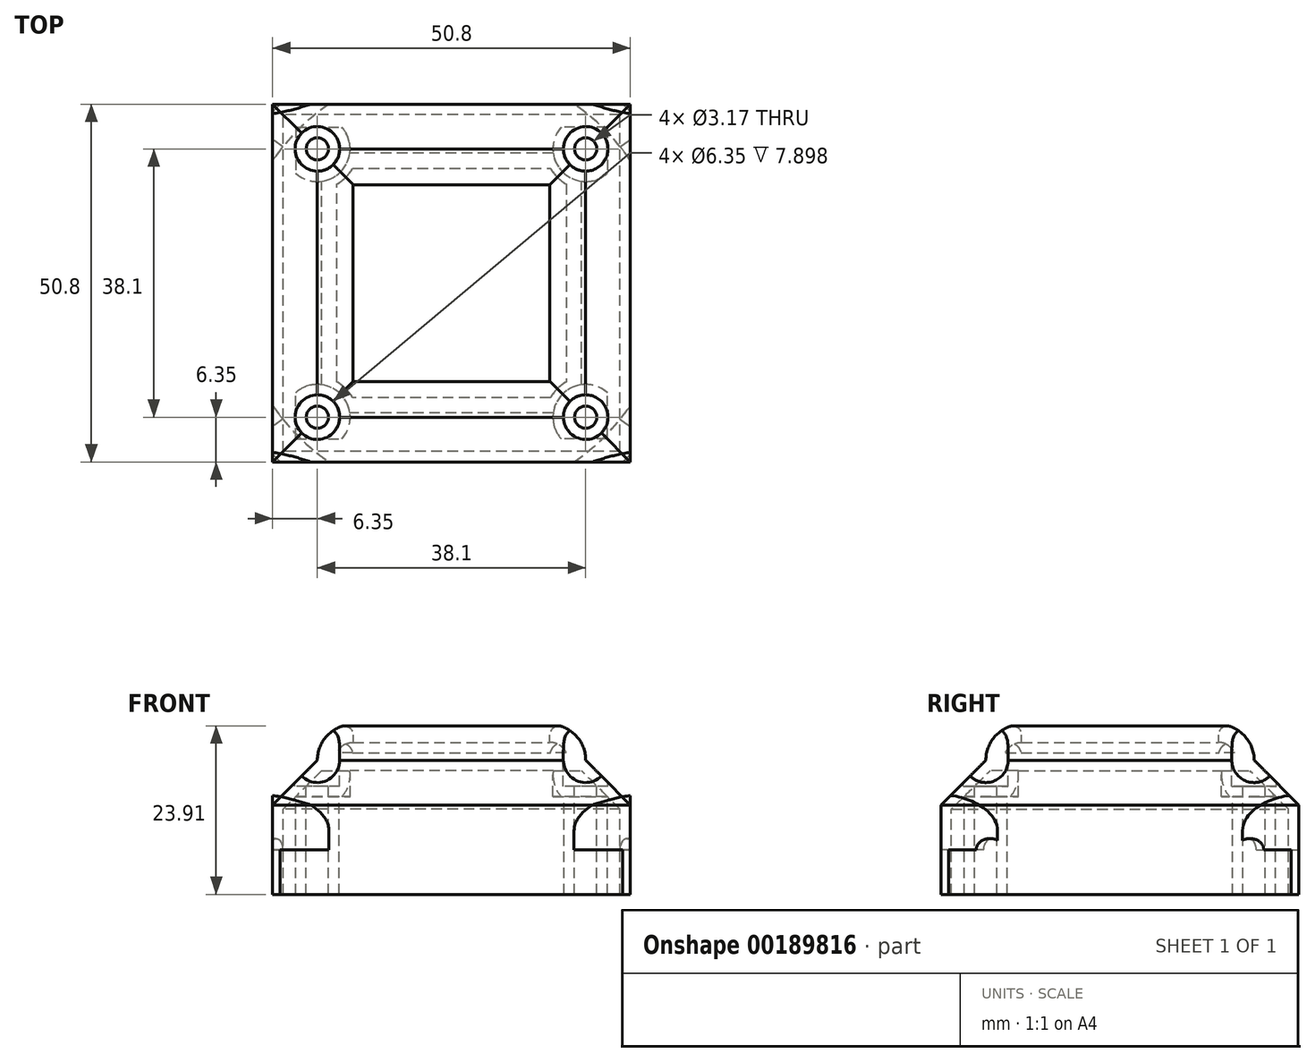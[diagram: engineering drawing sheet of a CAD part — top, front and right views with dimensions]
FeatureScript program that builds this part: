
annotation { "Feature Type Name" : "Feature", "Feature Type Description" : "" }
export const myFeature = defineFeature(function(context is Context, id is Id, definition is map)
    precondition{}
    {
        {
            var Q0;
            Q0=qCreatedBy(makeId("Front.planeOp"),FACE);
            var sketch = newSketch(context, id + "F0", { "sketchPlane" : qUnion([Q0])});
            skLineSegment(sketch, "E0.bottom", {"start": v(30.79, -7.77) * mm, "end": v(-30.79, -7.77) * mm});
            skLineSegment(sketch, "E0.top", {"start": v(30.79, 7.77) * mm, "end": v(-30.79, 7.77) * mm});
            skLineSegment(sketch, "E0.left", {"start": v(30.79, -7.77) * mm, "end": v(30.79, 7.77) * mm});
            skLineSegment(sketch, "E0.right", {"start": v(-30.79, -7.77) * mm, "end": v(-30.79, 7.77) * mm});
            skPoint(sketch, "E0.middle", {"position": v(0, 0) * mm});
            skLineSegment(sketch, "E1.bottom", {"start": v(30.79, 7.77) * mm, "end": v(39.54, 7.77) * mm});
            skLineSegment(sketch, "E1.top", {"start": v(30.79, -14.83) * mm, "end": v(39.54, -14.83) * mm});
            skLineSegment(sketch, "E1.left", {"start": v(30.79, 7.77) * mm, "end": v(30.79, -14.83) * mm});
            skLineSegment(sketch, "E1.right", {"start": v(39.54, 7.77) * mm, "end": v(39.54, -14.83) * mm});
            skLineSegment(sketch, "E2", {"start": v(30.79, -7.77) * mm, "end": v(39.54, -7.77) * mm});
            skLineSegment(sketch, "E3", {"start": v(0, 7.77) * mm, "end": v(0, -7.77) * mm});
            skLineSegment(sketch, "E4", {"start": v(-30.79, 0) * mm, "end": v(0, 0) * mm});
            skLineSegment(sketch, "E5", {"start": v(30.79, 0) * mm, "end": v(39.54, 0) * mm});
            skCircle(sketch, "E6", {"center": v(0, 0) * mm, "radius": 3.17 * mm});
            skLineSegment(sketch, "E7", {"start": v(35.16, 0) * mm, "end": v(35.16, -7.77) * mm});
            skLineSegment(sketch, "E8", {"start": v(39.54, -3.53) * mm, "end": v(35.16, -3.53) * mm});
            skSolve(sketch);
        }
        {
            var Q0;
            {var subQ1=sQuery(id+"F0.wireOp",EDGE,"E1.bottom");Q0=makeQuery(id+"F0.imprint","IMPRINT",FACE,{"disambiguationData":[TD([[makeQuery(id+"F0.imprint","IMPRINT",EDGE,{"derivedFrom":subQ1}),-1.0]])]});}
            var Q1;
            {var subQ5=sQuery(id+"F0.wireOp",EDGE,"E7");Q1=makeQuery(id+"F0.imprint","IMPRINT",FACE,{"disambiguationData":[TD([[makeQuery(id+"F0.imprint","IMPRINT",EDGE,{"derivedFrom":subQ5}),1.0]])]});}
            var Q2;
            {var subQ4=sQuery(id+"F0.wireOp",EDGE,"E1.top");Q2=makeQuery(id+"F0.imprint","IMPRINT",FACE,{"disambiguationData":[TD([[makeQuery(id+"F0.imprint","IMPRINT",EDGE,{"derivedFrom":subQ4}),1.0]])]});}
            var Q3;
            Q3=sQuery(id+"F0.wireOp",EDGE,"E3");
            revolve(context, id + "F1", {"entities" : qUnion([Q0, Q1, Q2]), "axis" : qUnion([Q3]), "revolveType" : RevolveType.SYMMETRIC, "angle" : 36 * degree});
        }
        {
            var Q0;
            {var subQ5=sQuery(id+"F0.wireOp",EDGE,"E1.bottom");Q0=makeQuery(id+"F0.imprint","IMPRINT",FACE,{"disambiguationData":[TD([[makeQuery(id+"F0.imprint","IMPRINT",EDGE,{"derivedFrom":subQ5}),-1.0]])]});}
            var Q1;
            {var subQ3=sQuery(id+"F0.wireOp",EDGE,"E8");Q1=makeQuery(id+"F0.imprint","IMPRINT",FACE,{"disambiguationData":[TD([[makeQuery(id+"F0.imprint","IMPRINT",EDGE,{"derivedFrom":subQ3}),-1.0]])]});}
            var Q2;
            {var subQ3=sQuery(id+"F0.wireOp",EDGE,"E8");Q2=makeQuery(id+"F0.imprint","IMPRINT",FACE,{"disambiguationData":[TD([[makeQuery(id+"F0.imprint","IMPRINT",EDGE,{"derivedFrom":subQ3}),1.0]])]});}
            var Q3;
            {var subQ5=sQuery(id+"F0.wireOp",EDGE,"E1.top");Q3=makeQuery(id+"F0.imprint","IMPRINT",FACE,{"disambiguationData":[TD([[makeQuery(id+"F0.imprint","IMPRINT",EDGE,{"derivedFrom":subQ5}),1.0]])]});}
            extrude(context, id + "F2", {"entities" : qUnion([Q0, Q1, Q2, Q3]), "endBound" : BoundingType.SYMMETRIC, "depth" : 25.4 * mm});
        }
        {
            var Q0;
            Q0=makeQuery(id+"F2.opExtrude","SWEPT_FACE",FACE,{"disambiguationData":[OSD([sQuery(id+"F0.wireOp",EDGE,"E1.right")])]});
            var sketch = newSketch(context, id + "F3", { "sketchPlane" : qUnion([Q0])});
            skCircle(sketch, "E9", {"center": v(0, 0) * mm, "radius": 2.98 * mm});
            skSolve(sketch);
        }
        {
            var Q0;
            Q0=sQuery(id+"F3.wireOp",VERTEX,"E9.center");
            var Q1;
            Q1=makeQuery(id+"F1.opRevolve","SWEPT_BODY",BODY,{"disambiguationData":[OSD([sQuery(id+"F0.wireOp",EDGE,"E1.bottom"),sQuery(id+"F0.wireOp",EDGE,"E1.top"),sQuery(id+"F0.wireOp",EDGE,"E1.left"),sQuery(id+"F0.wireOp",EDGE,"E1.right"),sQuery(id+"F0.wireOp",EDGE,"E2"),sQuery(id+"F0.wireOp",EDGE,"E5"),sQuery(id+"F0.wireOp",EDGE,"E7")])]});
            hole(context, id + "F4", {"style" : HoleStyle.C_BORE, "endStyle" : HoleEndStyle.BLIND, "holeDiameter" : 3.17 * mm, "cBoreDiameter" : 6.35 * mm, "cBoreDepth" : 0.5 * mm, "holeDepth" : 12.7 * mm, "locations" : qUnion([Q0]), "scope" : qUnion([Q1])});
        }
        {
            var Q0;
            Q0=makeQuery(id+"F1.opRevolve","SWEPT_BODY",BODY,{"disambiguationData":[OSD([sQuery(id+"F0.wireOp",EDGE,"E1.bottom"),sQuery(id+"F0.wireOp",EDGE,"E1.top"),sQuery(id+"F0.wireOp",EDGE,"E1.left"),sQuery(id+"F0.wireOp",EDGE,"E1.right"),sQuery(id+"F0.wireOp",EDGE,"E2"),sQuery(id+"F0.wireOp",EDGE,"E5"),sQuery(id+"F0.wireOp",EDGE,"E7")])]});
            var Q1;
            Q1=sQuery(id+"F0.wireOp",EDGE,"E3");
            circularPattern(context, id + "F5", {"operationType" : NewBodyOperationType.ADD, "entities" : qUnion([Q0]), "axis" : qUnion([Q1]), "angle" : 36 * degree, "instanceCount" : 10});
        }
        {
            var Q0;
            {var subQ0=makeQuery(id+"F1.opRevolve","SWEPT_EDGE",EDGE,{"disambiguationData":[OSD([sQuery(id+"F0.wireOp",EDGE,"E1.bottom"),sQuery(id+"F0.wireOp",EDGE,"E1.right")])]});Q0=makeQuery(id+"F5.boolean.opBoolean","MERGE",EDGE,{"derivedFrom":[subQ0,makeQuery(id+"F5.opPattern","COPY",EDGE,{"derivedFrom":subQ0,"instanceName":"1"}),makeQuery(id+"F5.opPattern","COPY",EDGE,{"derivedFrom":subQ0,"instanceName":"2"}),makeQuery(id+"F5.opPattern","COPY",EDGE,{"derivedFrom":subQ0,"instanceName":"3"}),makeQuery(id+"F5.opPattern","COPY",EDGE,{"derivedFrom":subQ0,"instanceName":"4"}),makeQuery(id+"F5.opPattern","COPY",EDGE,{"derivedFrom":subQ0,"instanceName":"5"}),makeQuery(id+"F5.opPattern","COPY",EDGE,{"derivedFrom":subQ0,"instanceName":"6"}),makeQuery(id+"F5.opPattern","COPY",EDGE,{"derivedFrom":subQ0,"instanceName":"7"}),makeQuery(id+"F5.opPattern","COPY",EDGE,{"derivedFrom":subQ0,"instanceName":"8"}),makeQuery(id+"F5.opPattern","COPY",EDGE,{"derivedFrom":subQ0,"instanceName":"9"})]});}
            chamfer(context, id + "F6", {"entities" : qUnion([Q0]), "width" : 1.27 * mm, "tangentPropagation" : true});
        }
        {
            var Q0;
            {var subQ0=makeQuery(id+"F1.opRevolve","SWEPT_EDGE",EDGE,{"disambiguationData":[OSD([sQuery(id+"F0.wireOp",EDGE,"E1.top"),sQuery(id+"F0.wireOp",EDGE,"E1.right")])]});Q0=makeQuery(id+"F5.boolean.opBoolean","MERGE",EDGE,{"derivedFrom":[subQ0,makeQuery(id+"F5.opPattern","COPY",EDGE,{"derivedFrom":subQ0,"instanceName":"1"}),makeQuery(id+"F5.opPattern","COPY",EDGE,{"derivedFrom":subQ0,"instanceName":"2"}),makeQuery(id+"F5.opPattern","COPY",EDGE,{"derivedFrom":subQ0,"instanceName":"3"}),makeQuery(id+"F5.opPattern","COPY",EDGE,{"derivedFrom":subQ0,"instanceName":"4"}),makeQuery(id+"F5.opPattern","COPY",EDGE,{"derivedFrom":subQ0,"instanceName":"5"}),makeQuery(id+"F5.opPattern","COPY",EDGE,{"derivedFrom":subQ0,"instanceName":"6"}),makeQuery(id+"F5.opPattern","COPY",EDGE,{"derivedFrom":subQ0,"instanceName":"7"}),makeQuery(id+"F5.opPattern","COPY",EDGE,{"derivedFrom":subQ0,"instanceName":"8"}),makeQuery(id+"F5.opPattern","COPY",EDGE,{"derivedFrom":subQ0,"instanceName":"9"})]});}
            chamfer(context, id + "F7", {"entities" : qUnion([Q0]), "width" : 8.13 * mm, "tangentPropagation" : true});
        }
        {
            var Q0;
            {var subQ0=makeQuery(id+"F1.opRevolve","SWEPT_EDGE",EDGE,{"disambiguationData":[OSD([sQuery(id+"F0.wireOp",EDGE,"E0.top"),sQuery(id+"F0.wireOp",EDGE,"E1.bottom"),sQuery(id+"F0.wireOp",EDGE,"E1.left")])]});Q0=makeQuery(id+"F5.boolean.opBoolean","MERGE",EDGE,{"derivedFrom":[subQ0,makeQuery(id+"F5.opPattern","COPY",EDGE,{"derivedFrom":subQ0,"instanceName":"1"}),makeQuery(id+"F5.opPattern","COPY",EDGE,{"derivedFrom":subQ0,"instanceName":"2"}),makeQuery(id+"F5.opPattern","COPY",EDGE,{"derivedFrom":subQ0,"instanceName":"3"}),makeQuery(id+"F5.opPattern","COPY",EDGE,{"derivedFrom":subQ0,"instanceName":"4"}),makeQuery(id+"F5.opPattern","COPY",EDGE,{"derivedFrom":subQ0,"instanceName":"5"}),makeQuery(id+"F5.opPattern","COPY",EDGE,{"derivedFrom":subQ0,"instanceName":"6"}),makeQuery(id+"F5.opPattern","COPY",EDGE,{"derivedFrom":subQ0,"instanceName":"7"}),makeQuery(id+"F5.opPattern","COPY",EDGE,{"derivedFrom":subQ0,"instanceName":"8"}),makeQuery(id+"F5.opPattern","COPY",EDGE,{"derivedFrom":subQ0,"instanceName":"9"})]});}
            fillet(context, id + "F8", {"entities" : qUnion([Q0]), "radius" : 5.08 * mm, "tangentPropagation" : true, "allowEdgeOverflow" : false});
        }
        {
            var Q0;
            Q0=qCreatedBy(makeId("Front.planeOp"),FACE);
            var sketch = newSketch(context, id + "F9", { "sketchPlane" : qUnion([Q0])});
            skLineSegment(sketch, "E10.bottom", {"start": v(25.4, -6.35) * mm, "end": v(-25.4, -6.35) * mm});
            skLineSegment(sketch, "E10.top", {"start": v(25.4, 6.35) * mm, "end": v(-25.4, 6.35) * mm});
            skLineSegment(sketch, "E10.left", {"start": v(25.4, -6.35) * mm, "end": v(25.4, 6.35) * mm});
            skLineSegment(sketch, "E10.right", {"start": v(-25.4, -6.35) * mm, "end": v(-25.4, 6.35) * mm});
            skPoint(sketch, "E10.middle", {"position": v(0, 0) * mm});
            skLineSegment(sketch, "E11", {"start": v(-25.4, 6.35) * mm, "end": v(-19.05, 12.7) * mm});
            skLineSegment(sketch, "E12", {"start": v(-19.05, 12.7) * mm, "end": v(19.05, 12.7) * mm});
            skLineSegment(sketch, "E13", {"start": v(19.05, 12.7) * mm, "end": v(25.4, 6.35) * mm});
            skSolve(sketch);
        }
        {
            var Q0;
            Q0=makeQuery(id+"F9.imprint","IMPRINT",FACE,{"disambiguationData":[TD([[makeQuery(id+"F9.imprint","IMPRINT",EDGE,{"derivedFrom":sQuery(id+"F9.wireOp",EDGE,"E10.bottom")}),-1.0]])]});
            var Q1;
            Q1=makeQuery(id+"F9.imprint","IMPRINT",FACE,{"disambiguationData":[TD([[makeQuery(id+"F9.imprint","IMPRINT",EDGE,{"derivedFrom":sQuery(id+"F9.wireOp",EDGE,"E10.top")}),-1.0]])]});
            extrude(context, id + "F10", {"entities" : qUnion([Q0, Q1]), "endBound" : BoundingType.SYMMETRIC, "depth" : 50.8 * mm});
        }
        {
            var Q0;
            Q0=qCreatedBy(makeId("Right.planeOp"),FACE);
            var sketch = newSketch(context, id + "F11", { "sketchPlane" : qUnion([Q0])});
            skLineSegment(sketch, "E14.bottom", {"start": v(25.4, -6.35) * mm, "end": v(-25.4, -6.35) * mm});
            skLineSegment(sketch, "E14.top", {"start": v(25.4, 6.35) * mm, "end": v(-25.4, 6.35) * mm});
            skLineSegment(sketch, "E14.left", {"start": v(25.4, -6.35) * mm, "end": v(25.4, 6.35) * mm});
            skLineSegment(sketch, "E14.right", {"start": v(-25.4, -6.35) * mm, "end": v(-25.4, 6.35) * mm});
            skPoint(sketch, "E14.middle", {"position": v(0, 0) * mm});
            skLineSegment(sketch, "E15", {"start": v(-25.4, 6.35) * mm, "end": v(-19.05, 12.7) * mm});
            skLineSegment(sketch, "E16", {"start": v(-19.05, 12.7) * mm, "end": v(19.05, 12.7) * mm});
            skLineSegment(sketch, "E17", {"start": v(19.05, 12.7) * mm, "end": v(25.4, 6.35) * mm});
            skSolve(sketch);
        }
        {
            var Q0;
            Q0=makeQuery(id+"F11.imprint","IMPRINT",FACE,{"disambiguationData":[TD([[makeQuery(id+"F11.imprint","IMPRINT",EDGE,{"derivedFrom":sQuery(id+"F11.wireOp",EDGE,"E14.bottom")}),-1.0]])]});
            var Q1;
            Q1=makeQuery(id+"F11.imprint","IMPRINT",FACE,{"disambiguationData":[TD([[makeQuery(id+"F11.imprint","IMPRINT",EDGE,{"derivedFrom":sQuery(id+"F11.wireOp",EDGE,"E14.top")}),-1.0]])]});
            extrude(context, id + "F12", {"entities" : qUnion([Q0, Q1]), "operationType" : NewBodyOperationType.INTERSECT, "endBound" : BoundingType.SYMMETRIC, "depth" : 50.8 * mm});
        }
        {
            var Q0;
            Q0=makeQuery(id+"F10.opExtrude","SWEPT_FACE",FACE,{"disambiguationData":[OSD([sQuery(id+"F9.wireOp",EDGE,"E12")])]});
            var sketch = newSketch(context, id + "F13", { "sketchPlane" : qUnion([Q0])});
            skLineSegment(sketch, "E18", {"start": v(0, -19.05) * mm, "end": v(0, 0) * mm});
            skLineSegment(sketch, "E19", {"start": v(0, 0) * mm, "end": v(0, 19.05) * mm});
            skLineSegment(sketch, "E20", {"start": v(0, 19.05) * mm, "end": v(0, 0) * mm});
            skLineSegment(sketch, "E21", {"start": v(19.05, 0) * mm, "end": v(0, 0) * mm});
            skLineSegment(sketch, "E22", {"start": v(-19.05, 0) * mm, "end": v(0, 0) * mm});
            skLineSegment(sketch, "E23", {"start": v(0, -19.05) * mm, "end": v(-19.05, -19.05) * mm});
            skLineSegment(sketch, "E24", {"start": v(-19.05, -19.05) * mm, "end": v(-19.05, 0) * mm});
            skLineSegment(sketch, "E25", {"start": v(-19.05, 19.05) * mm, "end": v(-19.05, 0) * mm});
            skLineSegment(sketch, "E26", {"start": v(-19.05, 19.05) * mm, "end": v(0, 19.05) * mm});
            skLineSegment(sketch, "E27", {"start": v(0, 19.05) * mm, "end": v(19.05, 19.05) * mm});
            skLineSegment(sketch, "E28", {"start": v(0, -19.05) * mm, "end": v(19.05, -19.05) * mm});
            skSolve(sketch);
        }
        {
            var Q0;
            Q0=sQuery(id+"F13.wireOp",VERTEX,"E24.start");
            var Q1;
            Q1=sQuery(id+"F13.wireOp",VERTEX,"E28.end");
            var Q2;
            Q2=sQuery(id+"F13.wireOp",VERTEX,"E27.end");
            var Q3;
            Q3=sQuery(id+"F13.wireOp",VERTEX,"E26.start");
            var Q4;
            Q4=makeQuery(id+"F10.opExtrude","SWEPT_BODY",BODY,{"disambiguationData":[OSD([sQuery(id+"F9.wireOp",EDGE,"E10.bottom"),sQuery(id+"F9.wireOp",EDGE,"E10.left"),sQuery(id+"F9.wireOp",EDGE,"E10.right"),sQuery(id+"F9.wireOp",EDGE,"E11"),sQuery(id+"F9.wireOp",EDGE,"E12"),sQuery(id+"F9.wireOp",EDGE,"E13")])]});
            hole(context, id + "F14", {"style" : HoleStyle.C_BORE, "endStyle" : HoleEndStyle.THROUGH, "holeDiameter" : 3.17 * mm, "cBoreDiameter" : 6.35 * mm, "cBoreDepth" : 0.5 * mm, "locations" : qUnion([Q0, Q1, Q2, Q3]), "scope" : qUnion([Q4]), "isTappedThrough" : true});
        }
        {
            var Q0;
            Q0=makeQuery(id+"F10.opExtrude","SWEPT_FACE",FACE,{"disambiguationData":[OSD([sQuery(id+"F9.wireOp",EDGE,"E10.bottom")])]});
            shell(context, id + "F15", {"entities" : qUnion([Q0]), "thickness" : 1.47 * mm});
        }
        {
            var Q0;
            Q0=makeQuery(id+"F10.opExtrude","SWEPT_FACE",FACE,{"disambiguationData":[OSD([sQuery(id+"F9.wireOp",EDGE,"E12")])]});
            extrude(context, id + "F18", {"entities" : qUnion([Q0]), "operationType" : NewBodyOperationType.ADD, "depth" : 5.08 * mm});
        }
        {
            var Q0;
            Q0=makeQuery(id+"F18.opExtrude","CAP_EDGE",EDGE,{"disambiguationData":[OSD([sQuery(id+"F11.wireOp",EDGE,"E15"),sQuery(id+"F11.wireOp",EDGE,"E16")])],"isStart":false});
            var Q1;
            Q1=makeQuery(id+"F18.opExtrude","CAP_EDGE",EDGE,{"disambiguationData":[OSD([sQuery(id+"F9.wireOp",EDGE,"E12"),sQuery(id+"F9.wireOp",EDGE,"E13")])],"isStart":false});
            var Q2;
            Q2=makeQuery(id+"F18.opExtrude","CAP_EDGE",EDGE,{"disambiguationData":[OSD([sQuery(id+"F11.wireOp",EDGE,"E16"),sQuery(id+"F11.wireOp",EDGE,"E17")])],"isStart":false});
            var Q3;
            Q3=makeQuery(id+"F18.opExtrude","CAP_EDGE",EDGE,{"disambiguationData":[OSD([sQuery(id+"F9.wireOp",EDGE,"E11"),sQuery(id+"F9.wireOp",EDGE,"E12")])],"isStart":false});
            fillet(context, id + "F16", {"entities" : qUnion([Q0, Q1, Q2, Q3]), "radius" : 5.08 * mm, "tangentPropagation" : true, "allowEdgeOverflow" : false});
        }
        {
            var Q0;
            Q0=makeQuery(id+"F18.opExtrude","CAP_FACE",FACE,{"disambiguationData":[OSD([sQuery(id+"F9.wireOp",EDGE,"E12")])],"isStart":false});
            shell(context, id + "F19", {"entities" : qUnion([Q0]), "thickness" : 2.54 * mm});
        }
        {
            var Q0;
            Q0=makeQuery(id+"F16.opFillet","BLEND_EDGE",EDGE,{"blendedFrom":[makeQuery(id+"F18.opExtrude","CAP_EDGE",EDGE,{"disambiguationData":[OSD([sQuery(id+"F11.wireOp",EDGE,"E15"),sQuery(id+"F11.wireOp",EDGE,"E16")])],"isStart":false}),makeQuery(id+"F18.opExtrude","CAP_FACE",FACE,{"disambiguationData":[OSD([sQuery(id+"F9.wireOp",EDGE,"E12")])],"isStart":false})],"blendedInto":[makeQuery(id+"F18.opExtrude","CAP_FACE",FACE,{"disambiguationData":[OSD([sQuery(id+"F9.wireOp",EDGE,"E12")])],"isStart":false})]});
            var Q1;
            {var subQ0=sQuery(id+"F9.wireOp",EDGE,"E12");Q1=makeQuery(id+"F16.opFillet","BLEND_EDGE",EDGE,{"blendedFrom":[makeQuery(id+"F18.opExtrude","CAP_EDGE",EDGE,{"disambiguationData":[OSD([sQuery(id+"F9.wireOp",EDGE,"E11"),subQ0])],"isStart":false}),makeQuery(id+"F18.opExtrude","CAP_FACE",FACE,{"disambiguationData":[OSD([subQ0])],"isStart":false})],"blendedInto":[makeQuery(id+"F18.opExtrude","CAP_FACE",FACE,{"disambiguationData":[OSD([subQ0])],"isStart":false})]});}
            var Q2;
            Q2=makeQuery(id+"F16.opFillet","BLEND_EDGE",EDGE,{"blendedFrom":[makeQuery(id+"F18.opExtrude","CAP_EDGE",EDGE,{"disambiguationData":[OSD([sQuery(id+"F11.wireOp",EDGE,"E16"),sQuery(id+"F11.wireOp",EDGE,"E17")])],"isStart":false}),makeQuery(id+"F18.opExtrude","CAP_FACE",FACE,{"disambiguationData":[OSD([sQuery(id+"F9.wireOp",EDGE,"E12")])],"isStart":false})],"blendedInto":[makeQuery(id+"F18.opExtrude","CAP_FACE",FACE,{"disambiguationData":[OSD([sQuery(id+"F9.wireOp",EDGE,"E12")])],"isStart":false})]});
            var Q3;
            {var subQ0=sQuery(id+"F9.wireOp",EDGE,"E12");Q3=makeQuery(id+"F16.opFillet","BLEND_EDGE",EDGE,{"blendedFrom":[makeQuery(id+"F18.opExtrude","CAP_EDGE",EDGE,{"disambiguationData":[OSD([subQ0,sQuery(id+"F9.wireOp",EDGE,"E13")])],"isStart":false}),makeQuery(id+"F18.opExtrude","CAP_FACE",FACE,{"disambiguationData":[OSD([subQ0])],"isStart":false})],"blendedInto":[makeQuery(id+"F18.opExtrude","CAP_FACE",FACE,{"disambiguationData":[OSD([subQ0])],"isStart":false})]});}
            fillet(context, id + "F17", {"entities" : qUnion([Q0, Q1, Q2, Q3]), "radius" : 1.27 * mm, "tangentPropagation" : true, "allowEdgeOverflow" : false});
        }
    });
